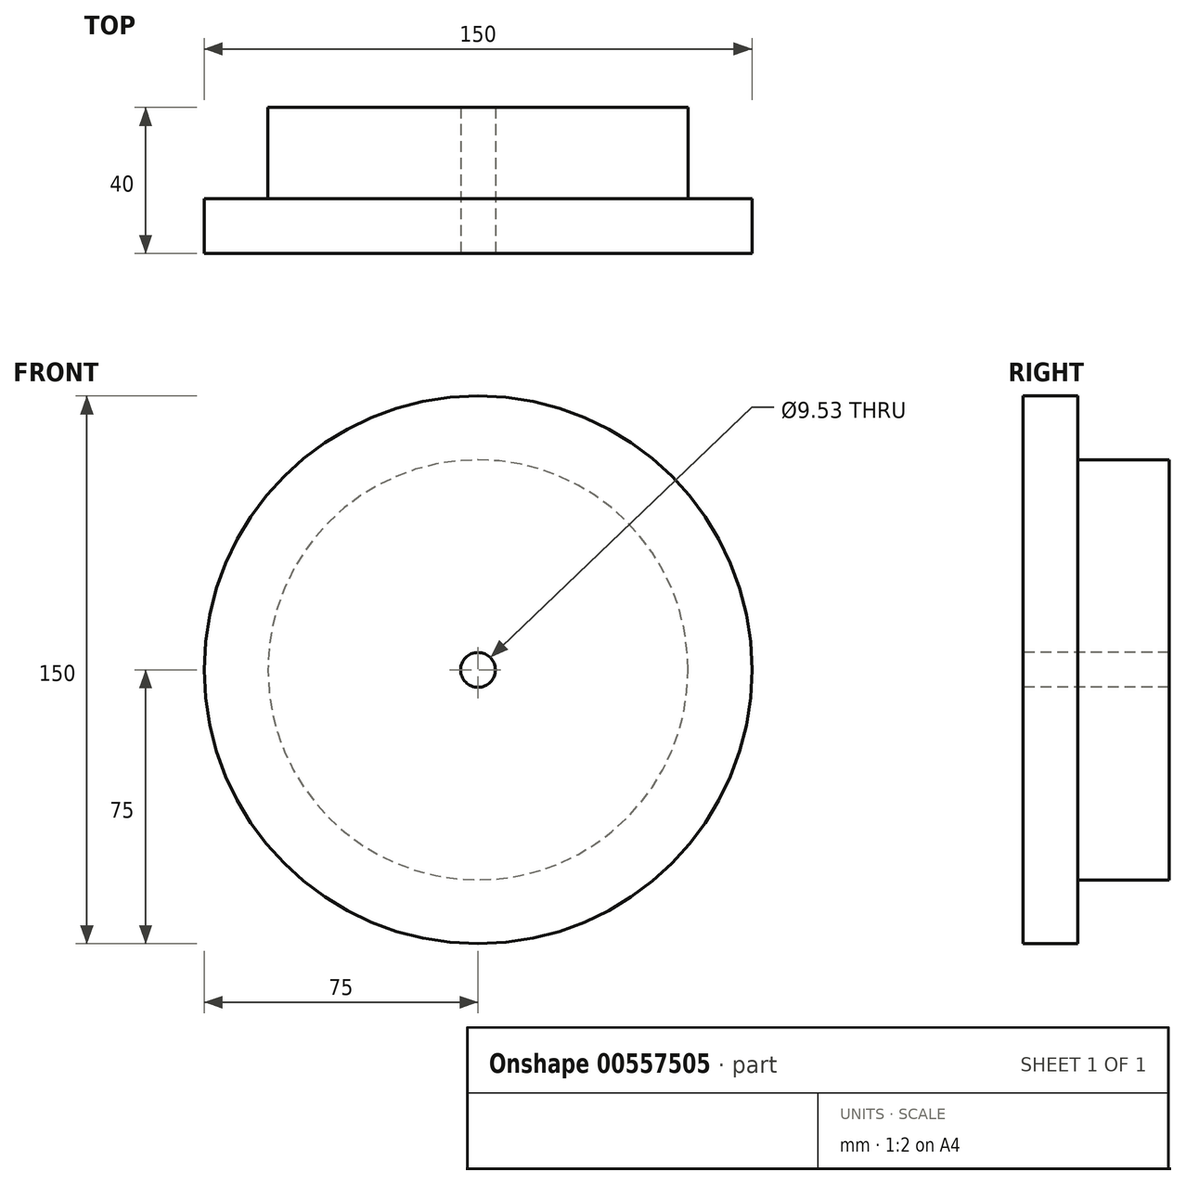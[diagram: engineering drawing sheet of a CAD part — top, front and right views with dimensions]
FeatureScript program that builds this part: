
annotation { "Feature Type Name" : "Feature", "Feature Type Description" : "" }
export const myFeature = defineFeature(function(context is Context, id is Id, definition is map)
    precondition{}
    {
        {
            var Q0;
            Q0=qCreatedBy(makeId("Front.planeOp"),FACE);
            var sketch = newSketch(context, id + "F0", { "sketchPlane" : qUnion([Q0])});
            skCircle(sketch, "E0", {"center": v(0, 0) * mm, "radius": 75 * mm});
            skSolve(sketch);
        }
        {
            var Q0;
            Q0 = qSketchRegion(id + "F0", true);
            extrude(context, id + "F1", {"entities" : qUnion([Q0]), "depth" : 15 * mm, "offsetDistance" : 25 * mm});
        }
        {
            var Q0;
            Q0=makeQuery(id+"F1.opExtrude","CAP_FACE",FACE,{"disambiguationData":[OSD([sQuery(id+"F0.wireOp",EDGE,"E0")])],"isStart":true});
            var sketch = newSketch(context, id + "F2", { "sketchPlane" : qUnion([Q0])});
            skCircle(sketch, "E1", {"center": v(0, 0) * mm, "radius": 57.5 * mm});
            skSolve(sketch);
        }
        {
            var Q0;
            Q0 = qSketchRegion(id + "F2", true);
            extrude(context, id + "F3", {"entities" : qUnion([Q0]), "operationType" : NewBodyOperationType.ADD, "depth" : 25 * mm, "offsetDistance" : 25 * mm});
        }
        {
            var Q0;
            Q0=makeQuery(id+"F1.opExtrude","CAP_FACE",FACE,{"disambiguationData":[OSD([sQuery(id+"F0.wireOp",EDGE,"E0")])],"isStart":false});
            var sketch = newSketch(context, id + "F4", { "sketchPlane" : qUnion([Q0])});
            skCircle(sketch, "E2", {"center": v(0, 0) * mm, "radius": 4.76 * mm});
            skSolve(sketch);
        }
        {
            var Q0;
            Q0 = qSketchRegion(id + "F4", true);
            extrude(context, id + "F5", {"entities" : qUnion([Q0]), "operationType" : NewBodyOperationType.REMOVE, "endBound" : BoundingType.THROUGH_ALL, "oppositeDirection" : true, "depth" : 25.4 * mm, "offsetDistance" : 25.4 * mm});
        }
    });
